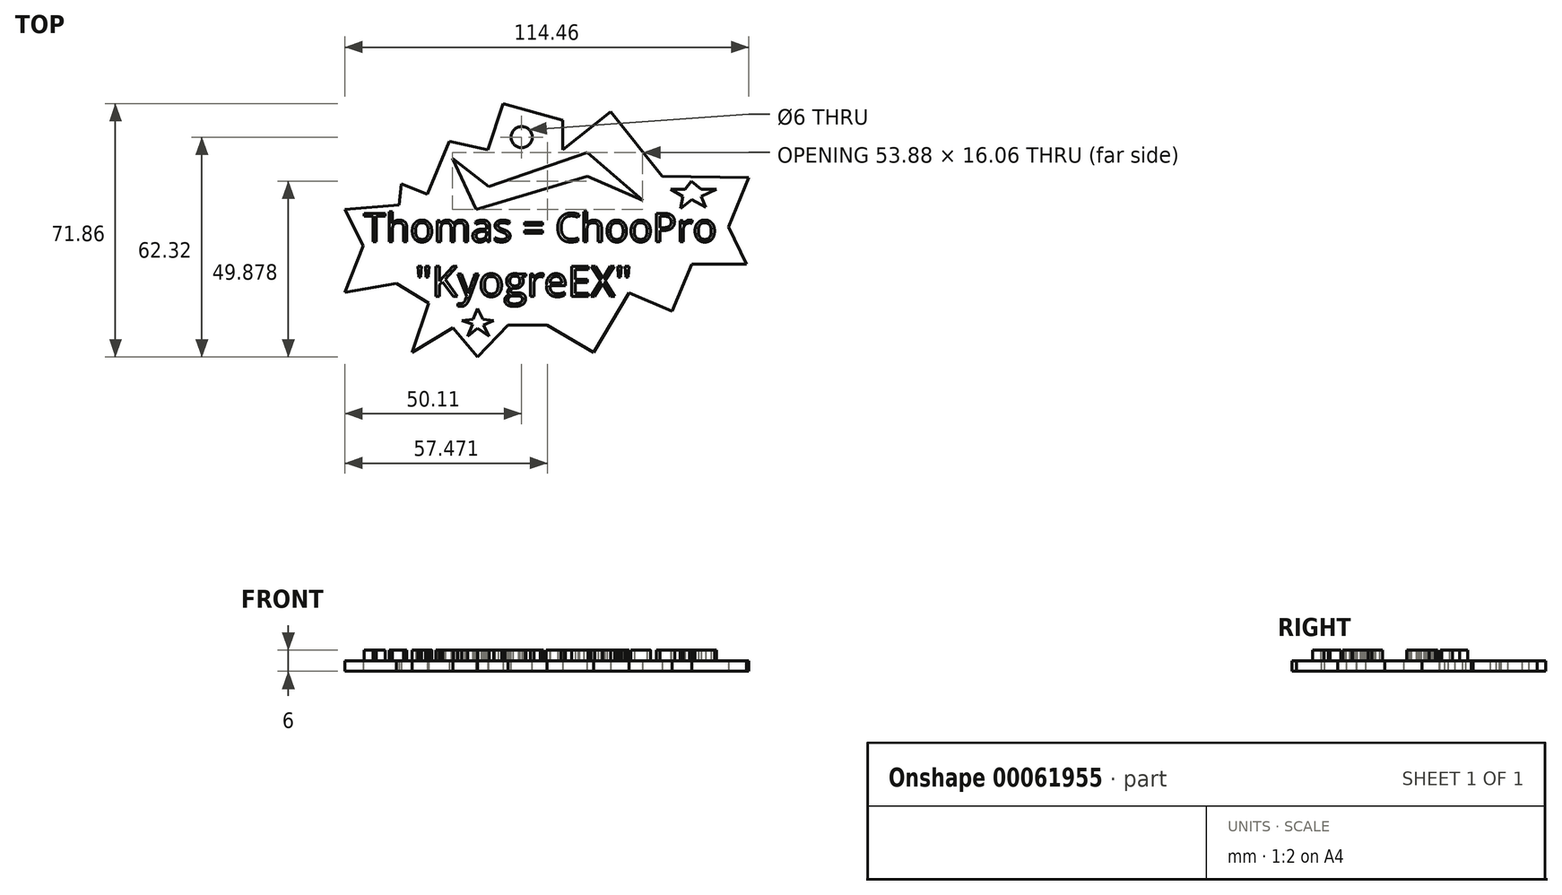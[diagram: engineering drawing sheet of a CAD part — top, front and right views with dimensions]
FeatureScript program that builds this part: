
annotation { "Feature Type Name" : "Feature", "Feature Type Description" : "" }
export const myFeature = defineFeature(function(context is Context, id is Id, definition is map)
    precondition{}
    {
        {
            var Q0;
            Q0=qCreatedBy(makeId("Top.planeOp"),FACE);
            var sketch = newSketch(context, id + "F0", { "sketchPlane" : qUnion([Q0])});
            skLineSegment(sketch, "E0", {"start": v(-34.28, 16.85) * mm, "end": v(-33.55, 22.8) * mm});
            skLineSegment(sketch, "E1", {"start": v(-33.55, 22.8) * mm, "end": v(-26.2, 19.79) * mm});
            skLineSegment(sketch, "E2", {"start": v(-26.2, 19.79) * mm, "end": v(-20.05, 34.77) * mm});
            skLineSegment(sketch, "E3", {"start": v(-20.05, 34.77) * mm, "end": v(-9.05, 32.38) * mm});
            skLineSegment(sketch, "E4", {"start": v(-9.05, 32.38) * mm, "end": v(-4.74, 45.54) * mm});
            skLineSegment(sketch, "E5", {"start": v(-4.74, 45.54) * mm, "end": v(12.13, 40.8) * mm});
            skLineSegment(sketch, "E6", {"start": v(12.13, 40.8) * mm, "end": v(12.13, 32.38) * mm});
            skLineSegment(sketch, "E7", {"start": v(12.13, 32.38) * mm, "end": v(25.73, 43.23) * mm});
            skLineSegment(sketch, "E8", {"start": v(48.76, 0) * mm, "end": v(43.07, -13.3) * mm});
            skLineSegment(sketch, "E9", {"start": v(30.87, -8.08) * mm, "end": v(43.07, -13.3) * mm});
            skLineSegment(sketch, "E10", {"start": v(30.87, -8.08) * mm, "end": v(20.86, -25.02) * mm});
            skLineSegment(sketch, "E11", {"start": v(7.63, -17.2) * mm, "end": v(20.86, -25.02) * mm});
            skLineSegment(sketch, "E12", {"start": v(7.63, -17.2) * mm, "end": v(-3.33, -17.2) * mm});
            skLineSegment(sketch, "E13", {"start": v(-3.33, -17.2) * mm, "end": v(-12.04, -26.32) * mm});
            skLineSegment(sketch, "E14", {"start": v(-12.04, -26.32) * mm, "end": v(-19, -18.04) * mm});
            skLineSegment(sketch, "E15", {"start": v(-19, -18.04) * mm, "end": v(-30.54, -25) * mm});
            skLineSegment(sketch, "E16", {"start": v(-30.54, -25) * mm, "end": v(-25.83, -10.97) * mm});
            skLineSegment(sketch, "E17", {"start": v(-25.83, -10.97) * mm, "end": v(-35.05, -5.49) * mm});
            skLineSegment(sketch, "E18", {"start": v(-35.05, -5.49) * mm, "end": v(-49.59, -7.94) * mm});
            skLineSegment(sketch, "E19", {"start": v(-49.59, -7.94) * mm, "end": v(-44.45, 5.28) * mm});
            skLineSegment(sketch, "E20", {"start": v(-44.45, 5.28) * mm, "end": v(-49.6, 15.56) * mm});
            skLineSegment(sketch, "E21", {"start": v(-49.6, 15.56) * mm, "end": v(-34.28, 16.85) * mm});
            skLineSegment(sketch, "E22", {"start": v(25.73, 43.23) * mm, "end": v(40.3, 24.96) * mm});
            skLineSegment(sketch, "E23", {"start": v(40.3, 24.96) * mm, "end": v(64.85, 24.57) * mm});
            skLineSegment(sketch, "E24", {"start": v(64.85, 24.57) * mm, "end": v(59.1, 10.54) * mm});
            skLineSegment(sketch, "E25", {"start": v(59.1, 10.54) * mm, "end": v(64.23, 0) * mm});
            skLineSegment(sketch, "E26", {"start": v(64.23, 0) * mm, "end": v(48.76, 0) * mm});
            skSolve(sketch);
        }
        {
            var Q0;
            Q0 = qSketchRegion(id + "F0", true);
            extrude(context, id + "F1", {"entities" : qUnion([Q0]), "depth" : 3 * mm});
        }
        {
            var Q0;
            Q0=makeQuery(id+"F1.opExtrude","CAP_FACE",FACE,{"disambiguationData":[OSD([sQuery(id+"F0.wireOp",EDGE,"E0"),sQuery(id+"F0.wireOp",EDGE,"E1"),sQuery(id+"F0.wireOp",EDGE,"E2"),sQuery(id+"F0.wireOp",EDGE,"E3"),sQuery(id+"F0.wireOp",EDGE,"E4"),sQuery(id+"F0.wireOp",EDGE,"E5"),sQuery(id+"F0.wireOp",EDGE,"E6"),sQuery(id+"F0.wireOp",EDGE,"E7"),sQuery(id+"F0.wireOp",EDGE,"E8"),sQuery(id+"F0.wireOp",EDGE,"E9"),sQuery(id+"F0.wireOp",EDGE,"E10"),sQuery(id+"F0.wireOp",EDGE,"E11"),sQuery(id+"F0.wireOp",EDGE,"E12"),sQuery(id+"F0.wireOp",EDGE,"E13"),sQuery(id+"F0.wireOp",EDGE,"E14"),sQuery(id+"F0.wireOp",EDGE,"E15"),sQuery(id+"F0.wireOp",EDGE,"E16"),sQuery(id+"F0.wireOp",EDGE,"E17"),sQuery(id+"F0.wireOp",EDGE,"E18"),sQuery(id+"F0.wireOp",EDGE,"E19"),sQuery(id+"F0.wireOp",EDGE,"E20"),sQuery(id+"F0.wireOp",EDGE,"E21"),sQuery(id+"F0.wireOp",EDGE,"E22"),sQuery(id+"F0.wireOp",EDGE,"E23"),sQuery(id+"F0.wireOp",EDGE,"E24"),sQuery(id+"F0.wireOp",EDGE,"E25"),sQuery(id+"F0.wireOp",EDGE,"E26")])],"isStart":false});
            var sketch = newSketch(context, id + "F2", { "sketchPlane" : qUnion([Q0])});
            skText(sketch, "E27", { "text": "Thomas = ChooPro", "fontName": "OpenSans-Regular.ttf"});
            skText(sketch, "E28", { "text": "\"KyogreEX\"", "fontName": "OpenSans-Regular.ttf"});
            const initialGuessF2  = {"E27": [-0.04426, 0.00638, 1, 0, 0.0081], "E28": [-0.02969, -0.00912, 1, 0, 0.00854]};
            skSetInitialGuess(sketch, initialGuessF2);
            skSolve(sketch);
        }
        {
            var Q0;
            Q0 = qSketchRegion(id + "F2", true);
            extrude(context, id + "F3", {"entities" : qUnion([Q0]), "operationType" : NewBodyOperationType.ADD, "depth" : 3 * mm});
        }
        {
            var Q0;
            {var subQ0=sQuery(id+"F0.wireOp",EDGE,"E17");var subQ1=sQuery(id+"F0.wireOp",EDGE,"E26");var subQ2=sQuery(id+"F0.wireOp",EDGE,"E9");var subQ3=sQuery(id+"F0.wireOp",EDGE,"E23");var subQ4=sQuery(id+"F0.wireOp",EDGE,"E24");var subQ5=sQuery(id+"F0.wireOp",EDGE,"E25");var subQ6=sQuery(id+"F0.wireOp",EDGE,"E22");var subQ7=sQuery(id+"F0.wireOp",EDGE,"E7");var subQ8=sQuery(id+"F0.wireOp",EDGE,"E14");var subQ9=sQuery(id+"F0.wireOp",EDGE,"E1");var subQ10=sQuery(id+"F0.wireOp",EDGE,"E6");var subQ11=sQuery(id+"F0.wireOp",EDGE,"E8");var subQ12=sQuery(id+"F0.wireOp",EDGE,"E5");var subQ13=sQuery(id+"F0.wireOp",EDGE,"E4");var subQ14=sQuery(id+"F0.wireOp",EDGE,"E0");var subQ15=sQuery(id+"F0.wireOp",EDGE,"E2");var subQ16=sQuery(id+"F0.wireOp",EDGE,"E3");var subQ17=sQuery(id+"F0.wireOp",EDGE,"E11");var subQ18=sQuery(id+"F0.wireOp",EDGE,"E16");var subQ19=sQuery(id+"F0.wireOp",EDGE,"E10");var subQ20=sQuery(id+"F0.wireOp",EDGE,"E18");var subQ21=sQuery(id+"F0.wireOp",EDGE,"E21");var subQ22=sQuery(id+"F0.wireOp",EDGE,"E19");var subQ23=sQuery(id+"F0.wireOp",EDGE,"E13");var subQ24=sQuery(id+"F0.wireOp",EDGE,"E12");var subQ25=sQuery(id+"F0.wireOp",EDGE,"E20");var subQ26=sQuery(id+"F0.wireOp",EDGE,"E15");Q0=makeQuery(id+"F3.boolean.opBoolean","SPLIT",FACE,{"disambiguationData":[TD([makeQuery(id+"F1.opExtrude","SWEPT_FACE",FACE,{"disambiguationData":[OSD([subQ14])]})])],"derivedFrom":makeQuery(id+"F1.opExtrude","CAP_FACE",FACE,{"disambiguationData":[OSD([subQ14,subQ9,subQ15,subQ16,subQ13,subQ12,subQ10,subQ7,subQ11,subQ2,subQ19,subQ17,subQ24,subQ23,subQ8,subQ26,subQ18,subQ0,subQ20,subQ22,subQ25,subQ21,subQ6,subQ3,subQ4,subQ5,subQ1])],"isStart":false})});}
            var sketch = newSketch(context, id + "F4", { "sketchPlane" : qUnion([Q0])});
            skLineSegment(sketch, "E29", {"start": v(-19.08, 30) * mm, "end": v(-12.4, 15.53) * mm});
            skLineSegment(sketch, "E30", {"start": v(-12.4, 15.53) * mm, "end": v(19.13, 24.9) * mm});
            skLineSegment(sketch, "E31", {"start": v(19.13, 24.9) * mm, "end": v(34.8, 18.07) * mm});
            skLineSegment(sketch, "E32", {"start": v(34.8, 18.07) * mm, "end": v(19.13, 31.59) * mm});
            skLineSegment(sketch, "E33", {"start": v(19.13, 31.59) * mm, "end": v(-8.85, 22.04) * mm});
            skLineSegment(sketch, "E34", {"start": v(-8.85, 22.04) * mm, "end": v(-19.08, 30) * mm});
            skSolve(sketch);
        }
        {
            var Q0;
            Q0 = qSketchRegion(id + "F4", true);
            var Q1;
            Q1=makeQuery(id+"F1.opExtrude","CAP_FACE",FACE,{"disambiguationData":[OSD([sQuery(id+"F0.wireOp",EDGE,"E0"),sQuery(id+"F0.wireOp",EDGE,"E1"),sQuery(id+"F0.wireOp",EDGE,"E2"),sQuery(id+"F0.wireOp",EDGE,"E3"),sQuery(id+"F0.wireOp",EDGE,"E4"),sQuery(id+"F0.wireOp",EDGE,"E5"),sQuery(id+"F0.wireOp",EDGE,"E6"),sQuery(id+"F0.wireOp",EDGE,"E7"),sQuery(id+"F0.wireOp",EDGE,"E8"),sQuery(id+"F0.wireOp",EDGE,"E9"),sQuery(id+"F0.wireOp",EDGE,"E10"),sQuery(id+"F0.wireOp",EDGE,"E11"),sQuery(id+"F0.wireOp",EDGE,"E12"),sQuery(id+"F0.wireOp",EDGE,"E13"),sQuery(id+"F0.wireOp",EDGE,"E14"),sQuery(id+"F0.wireOp",EDGE,"E15"),sQuery(id+"F0.wireOp",EDGE,"E16"),sQuery(id+"F0.wireOp",EDGE,"E17"),sQuery(id+"F0.wireOp",EDGE,"E18"),sQuery(id+"F0.wireOp",EDGE,"E19"),sQuery(id+"F0.wireOp",EDGE,"E20"),sQuery(id+"F0.wireOp",EDGE,"E21"),sQuery(id+"F0.wireOp",EDGE,"E22"),sQuery(id+"F0.wireOp",EDGE,"E23"),sQuery(id+"F0.wireOp",EDGE,"E24"),sQuery(id+"F0.wireOp",EDGE,"E25"),sQuery(id+"F0.wireOp",EDGE,"E26")])],"isStart":true});
            extrude(context, id + "F5", {"entities" : qUnion([Q0]), "operationType" : NewBodyOperationType.REMOVE, "endBound" : BoundingType.UP_TO_SURFACE, "oppositeDirection" : true, "endBoundEntityFace" : qUnion([Q1]), "depth" : 25 * mm});
        }
        {
            var Q0;
            {var subQ0=sQuery(id+"F0.wireOp",EDGE,"E17");var subQ1=sQuery(id+"F0.wireOp",EDGE,"E26");var subQ2=sQuery(id+"F0.wireOp",EDGE,"E9");var subQ3=sQuery(id+"F0.wireOp",EDGE,"E23");var subQ4=sQuery(id+"F0.wireOp",EDGE,"E24");var subQ5=sQuery(id+"F0.wireOp",EDGE,"E25");var subQ6=sQuery(id+"F0.wireOp",EDGE,"E22");var subQ7=sQuery(id+"F0.wireOp",EDGE,"E7");var subQ8=sQuery(id+"F0.wireOp",EDGE,"E14");var subQ9=sQuery(id+"F0.wireOp",EDGE,"E1");var subQ10=sQuery(id+"F0.wireOp",EDGE,"E6");var subQ11=sQuery(id+"F0.wireOp",EDGE,"E8");var subQ12=sQuery(id+"F0.wireOp",EDGE,"E5");var subQ13=sQuery(id+"F0.wireOp",EDGE,"E4");var subQ14=sQuery(id+"F0.wireOp",EDGE,"E0");var subQ15=sQuery(id+"F0.wireOp",EDGE,"E2");var subQ16=sQuery(id+"F0.wireOp",EDGE,"E3");var subQ17=sQuery(id+"F0.wireOp",EDGE,"E11");var subQ18=sQuery(id+"F0.wireOp",EDGE,"E16");var subQ19=sQuery(id+"F0.wireOp",EDGE,"E10");var subQ20=sQuery(id+"F0.wireOp",EDGE,"E18");var subQ21=sQuery(id+"F0.wireOp",EDGE,"E21");var subQ22=sQuery(id+"F0.wireOp",EDGE,"E19");var subQ23=sQuery(id+"F0.wireOp",EDGE,"E13");var subQ24=sQuery(id+"F0.wireOp",EDGE,"E12");var subQ25=sQuery(id+"F0.wireOp",EDGE,"E20");var subQ26=sQuery(id+"F0.wireOp",EDGE,"E15");Q0=makeQuery(id+"F3.boolean.opBoolean","SPLIT",FACE,{"disambiguationData":[TD([makeQuery(id+"F1.opExtrude","SWEPT_FACE",FACE,{"disambiguationData":[OSD([subQ14])]})])],"derivedFrom":makeQuery(id+"F1.opExtrude","CAP_FACE",FACE,{"disambiguationData":[OSD([subQ14,subQ9,subQ15,subQ16,subQ13,subQ12,subQ10,subQ7,subQ11,subQ2,subQ19,subQ17,subQ24,subQ23,subQ8,subQ26,subQ18,subQ0,subQ20,subQ22,subQ25,subQ21,subQ6,subQ3,subQ4,subQ5,subQ1])],"isStart":false})});}
            var sketch = newSketch(context, id + "F6", { "sketchPlane" : qUnion([Q0])});
            skLineSegment(sketch, "E35", {"start": v(-13.27, -15.55) * mm, "end": v(-12, -12.5) * mm});
            skLineSegment(sketch, "E36", {"start": v(-12, -12.5) * mm, "end": v(-10.5, -15.55) * mm});
            skLineSegment(sketch, "E37", {"start": v(-10.5, -15.55) * mm, "end": v(-7.4, -15.97) * mm});
            skLineSegment(sketch, "E38", {"start": v(-7.4, -15.97) * mm, "end": v(-10.32, -17.22) * mm});
            skLineSegment(sketch, "E39", {"start": v(-10.32, -17.22) * mm, "end": v(-8.68, -20.4) * mm});
            skLineSegment(sketch, "E40", {"start": v(-8.68, -20.4) * mm, "end": v(-12, -18.16) * mm});
            skLineSegment(sketch, "E41", {"start": v(-12, -18.16) * mm, "end": v(-14.74, -20.4) * mm});
            skLineSegment(sketch, "E42", {"start": v(-14.74, -20.4) * mm, "end": v(-13.37, -17.05) * mm});
            skLineSegment(sketch, "E43", {"start": v(-13.37, -17.05) * mm, "end": v(-16.48, -15.97) * mm});
            skLineSegment(sketch, "E44", {"start": v(-16.48, -15.97) * mm, "end": v(-13.27, -15.55) * mm});
            skSolve(sketch);
        }
        {
            var Q0;
            Q0 = qSketchRegion(id + "F6", true);
            extrude(context, id + "F7", {"entities" : qUnion([Q0]), "operationType" : NewBodyOperationType.ADD, "depth" : 3 * mm});
        }
        {
            var Q0;
            {var subQ0=sQuery(id+"F0.wireOp",EDGE,"E17");var subQ1=sQuery(id+"F0.wireOp",EDGE,"E26");var subQ2=sQuery(id+"F0.wireOp",EDGE,"E9");var subQ3=sQuery(id+"F0.wireOp",EDGE,"E23");var subQ4=sQuery(id+"F0.wireOp",EDGE,"E24");var subQ5=sQuery(id+"F0.wireOp",EDGE,"E25");var subQ6=sQuery(id+"F0.wireOp",EDGE,"E22");var subQ7=sQuery(id+"F0.wireOp",EDGE,"E7");var subQ8=sQuery(id+"F0.wireOp",EDGE,"E14");var subQ9=sQuery(id+"F0.wireOp",EDGE,"E1");var subQ10=sQuery(id+"F0.wireOp",EDGE,"E6");var subQ11=sQuery(id+"F0.wireOp",EDGE,"E8");var subQ12=sQuery(id+"F0.wireOp",EDGE,"E5");var subQ13=sQuery(id+"F0.wireOp",EDGE,"E4");var subQ14=sQuery(id+"F0.wireOp",EDGE,"E0");var subQ15=sQuery(id+"F0.wireOp",EDGE,"E2");var subQ16=sQuery(id+"F0.wireOp",EDGE,"E3");var subQ17=sQuery(id+"F0.wireOp",EDGE,"E11");var subQ18=sQuery(id+"F0.wireOp",EDGE,"E16");var subQ19=sQuery(id+"F0.wireOp",EDGE,"E10");var subQ20=sQuery(id+"F0.wireOp",EDGE,"E18");var subQ21=sQuery(id+"F0.wireOp",EDGE,"E21");var subQ22=sQuery(id+"F0.wireOp",EDGE,"E19");var subQ23=sQuery(id+"F0.wireOp",EDGE,"E13");var subQ24=sQuery(id+"F0.wireOp",EDGE,"E12");var subQ25=sQuery(id+"F0.wireOp",EDGE,"E20");var subQ26=sQuery(id+"F0.wireOp",EDGE,"E15");Q0=makeQuery(id+"F3.boolean.opBoolean","SPLIT",FACE,{"disambiguationData":[TD([makeQuery(id+"F1.opExtrude","SWEPT_FACE",FACE,{"disambiguationData":[OSD([subQ14])]})])],"derivedFrom":makeQuery(id+"F1.opExtrude","CAP_FACE",FACE,{"disambiguationData":[OSD([subQ14,subQ9,subQ15,subQ16,subQ13,subQ12,subQ10,subQ7,subQ11,subQ2,subQ19,subQ17,subQ24,subQ23,subQ8,subQ26,subQ18,subQ0,subQ20,subQ22,subQ25,subQ21,subQ6,subQ3,subQ4,subQ5,subQ1])],"isStart":false})});}
            var sketch = newSketch(context, id + "F8", { "sketchPlane" : qUnion([Q0])});
            skCircle(sketch, "E45", {"center": v(0.5, 36) * mm, "radius": 3 * mm});
            skSolve(sketch);
        }
        {
            var Q0;
            Q0 = qSketchRegion(id + "F8", true);
            var Q1;
            Q1=makeQuery(id+"F1.opExtrude","CAP_FACE",FACE,{"disambiguationData":[OSD([sQuery(id+"F0.wireOp",EDGE,"E0"),sQuery(id+"F0.wireOp",EDGE,"E1"),sQuery(id+"F0.wireOp",EDGE,"E2"),sQuery(id+"F0.wireOp",EDGE,"E3"),sQuery(id+"F0.wireOp",EDGE,"E4"),sQuery(id+"F0.wireOp",EDGE,"E5"),sQuery(id+"F0.wireOp",EDGE,"E6"),sQuery(id+"F0.wireOp",EDGE,"E7"),sQuery(id+"F0.wireOp",EDGE,"E8"),sQuery(id+"F0.wireOp",EDGE,"E9"),sQuery(id+"F0.wireOp",EDGE,"E10"),sQuery(id+"F0.wireOp",EDGE,"E11"),sQuery(id+"F0.wireOp",EDGE,"E12"),sQuery(id+"F0.wireOp",EDGE,"E13"),sQuery(id+"F0.wireOp",EDGE,"E14"),sQuery(id+"F0.wireOp",EDGE,"E15"),sQuery(id+"F0.wireOp",EDGE,"E16"),sQuery(id+"F0.wireOp",EDGE,"E17"),sQuery(id+"F0.wireOp",EDGE,"E18"),sQuery(id+"F0.wireOp",EDGE,"E19"),sQuery(id+"F0.wireOp",EDGE,"E20"),sQuery(id+"F0.wireOp",EDGE,"E21"),sQuery(id+"F0.wireOp",EDGE,"E22"),sQuery(id+"F0.wireOp",EDGE,"E23"),sQuery(id+"F0.wireOp",EDGE,"E24"),sQuery(id+"F0.wireOp",EDGE,"E25"),sQuery(id+"F0.wireOp",EDGE,"E26")])],"isStart":true});
            extrude(context, id + "F9", {"entities" : qUnion([Q0]), "operationType" : NewBodyOperationType.REMOVE, "endBound" : BoundingType.UP_TO_SURFACE, "oppositeDirection" : true, "endBoundEntityFace" : qUnion([Q1]), "depth" : 25 * mm});
        }
        {
            var Q0;
            {var subQ0=sQuery(id+"F0.wireOp",EDGE,"E17");var subQ1=sQuery(id+"F0.wireOp",EDGE,"E26");var subQ2=sQuery(id+"F0.wireOp",EDGE,"E9");var subQ3=sQuery(id+"F0.wireOp",EDGE,"E23");var subQ4=sQuery(id+"F0.wireOp",EDGE,"E24");var subQ5=sQuery(id+"F0.wireOp",EDGE,"E25");var subQ6=sQuery(id+"F0.wireOp",EDGE,"E22");var subQ7=sQuery(id+"F0.wireOp",EDGE,"E7");var subQ8=sQuery(id+"F0.wireOp",EDGE,"E14");var subQ9=sQuery(id+"F0.wireOp",EDGE,"E1");var subQ10=sQuery(id+"F0.wireOp",EDGE,"E6");var subQ11=sQuery(id+"F0.wireOp",EDGE,"E8");var subQ12=sQuery(id+"F0.wireOp",EDGE,"E5");var subQ13=sQuery(id+"F0.wireOp",EDGE,"E4");var subQ14=sQuery(id+"F0.wireOp",EDGE,"E0");var subQ15=sQuery(id+"F0.wireOp",EDGE,"E2");var subQ16=sQuery(id+"F0.wireOp",EDGE,"E3");var subQ17=sQuery(id+"F0.wireOp",EDGE,"E11");var subQ18=sQuery(id+"F0.wireOp",EDGE,"E16");var subQ19=sQuery(id+"F0.wireOp",EDGE,"E10");var subQ20=sQuery(id+"F0.wireOp",EDGE,"E18");var subQ21=sQuery(id+"F0.wireOp",EDGE,"E21");var subQ22=sQuery(id+"F0.wireOp",EDGE,"E19");var subQ23=sQuery(id+"F0.wireOp",EDGE,"E13");var subQ24=sQuery(id+"F0.wireOp",EDGE,"E12");var subQ25=sQuery(id+"F0.wireOp",EDGE,"E20");var subQ26=sQuery(id+"F0.wireOp",EDGE,"E15");Q0=makeQuery(id+"F3.boolean.opBoolean","SPLIT",FACE,{"disambiguationData":[TD([makeQuery(id+"F1.opExtrude","SWEPT_FACE",FACE,{"disambiguationData":[OSD([subQ14])]})])],"derivedFrom":makeQuery(id+"F1.opExtrude","CAP_FACE",FACE,{"disambiguationData":[OSD([subQ14,subQ9,subQ15,subQ16,subQ13,subQ12,subQ10,subQ7,subQ11,subQ2,subQ19,subQ17,subQ24,subQ23,subQ8,subQ26,subQ18,subQ0,subQ20,subQ22,subQ25,subQ21,subQ6,subQ3,subQ4,subQ5,subQ1])],"isStart":false})});}
            var sketch = newSketch(context, id + "F10", { "sketchPlane" : qUnion([Q0])});
            skLineSegment(sketch, "E46", {"start": v(48.57, 23.55) * mm, "end": v(46.74, 21.18) * mm});
            skLineSegment(sketch, "E47", {"start": v(48.57, 23.55) * mm, "end": v(51.37, 21.18) * mm});
            skLineSegment(sketch, "E48", {"start": v(51.37, 21.18) * mm, "end": v(55.74, 21.2) * mm});
            skLineSegment(sketch, "E49", {"start": v(55.74, 21.2) * mm, "end": v(51.37, 19.15) * mm});
            skLineSegment(sketch, "E50", {"start": v(52.65, 16.17) * mm, "end": v(51.37, 19.15) * mm});
            skLineSegment(sketch, "E51", {"start": v(52.65, 16.17) * mm, "end": v(48.7, 18.3) * mm});
            skLineSegment(sketch, "E52", {"start": v(48.7, 18.3) * mm, "end": v(45.52, 15.75) * mm});
            skLineSegment(sketch, "E53", {"start": v(46.74, 21.18) * mm, "end": v(42.75, 21.18) * mm});
            skLineSegment(sketch, "E54", {"start": v(42.75, 21.18) * mm, "end": v(46.15, 19.15) * mm});
            skLineSegment(sketch, "E55", {"start": v(46.15, 19.15) * mm, "end": v(45.52, 15.75) * mm});
            skSolve(sketch);
        }
        {
            var Q0;
            Q0 = qSketchRegion(id + "F10", true);
            extrude(context, id + "F11", {"entities" : qUnion([Q0]), "operationType" : NewBodyOperationType.ADD, "depth" : 3 * mm});
        }
    });
